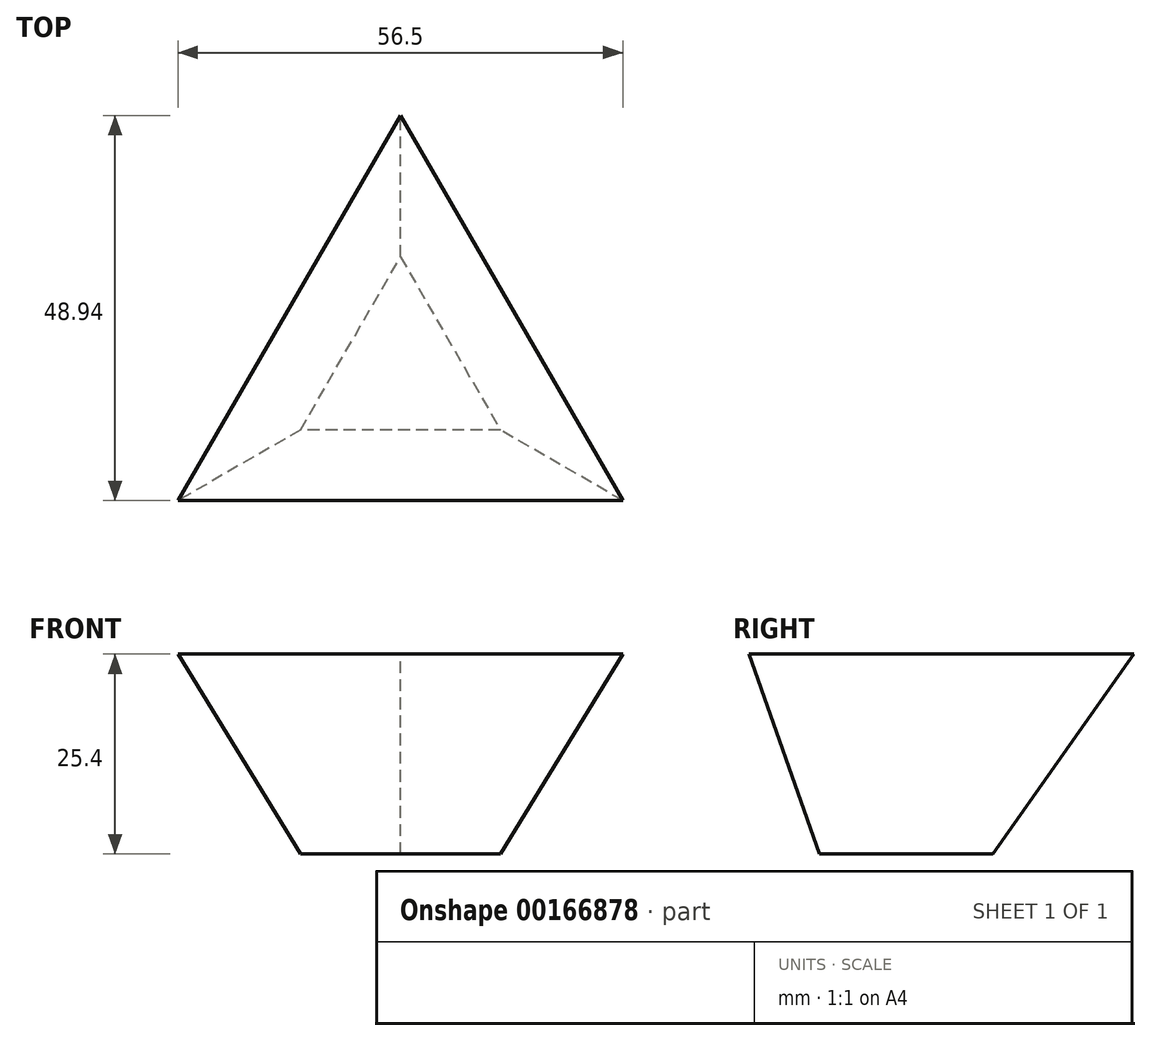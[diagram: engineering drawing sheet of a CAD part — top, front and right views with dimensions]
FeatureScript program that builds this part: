
annotation { "Feature Type Name" : "Feature", "Feature Type Description" : "" }
export const myFeature = defineFeature(function(context is Context, id is Id, definition is map)
    precondition{}
    {
        {
            var Q0;
            Q0=qCreatedBy(makeId("Top.planeOp"),FACE);
            var sketch = newSketch(context, id + "F0", { "sketchPlane" : qUnion([Q0])});
            skLineSegment(sketch, "E0", {"start": v(12.7, 0) * mm, "end": v(0, 22) * mm});
            skLineSegment(sketch, "E1", {"start": v(-12.7, 0) * mm, "end": v(0, 22) * mm});
            skLineSegment(sketch, "E2", {"start": v(-12.7, 0) * mm, "end": v(12.7, 0) * mm});
            skSolve(sketch);
        }
        {
            var Q0;
            Q0=makeQuery(id+"F0.imprint","IMPRINT",FACE,{"disambiguationData":[TD([[makeQuery(id+"F0.imprint","IMPRINT",EDGE,{"derivedFrom":sQuery(id+"F0.wireOp",EDGE,"E0")}),1.0]])]});
            extrude(context, id + "F1", {"entities" : qUnion([Q0]), "depth" : 25.4 * mm, "hasDraft" : true, "draftAngle" : 90 * degree - atan(2 * (2 ^ 0.5))});
        }
    });
